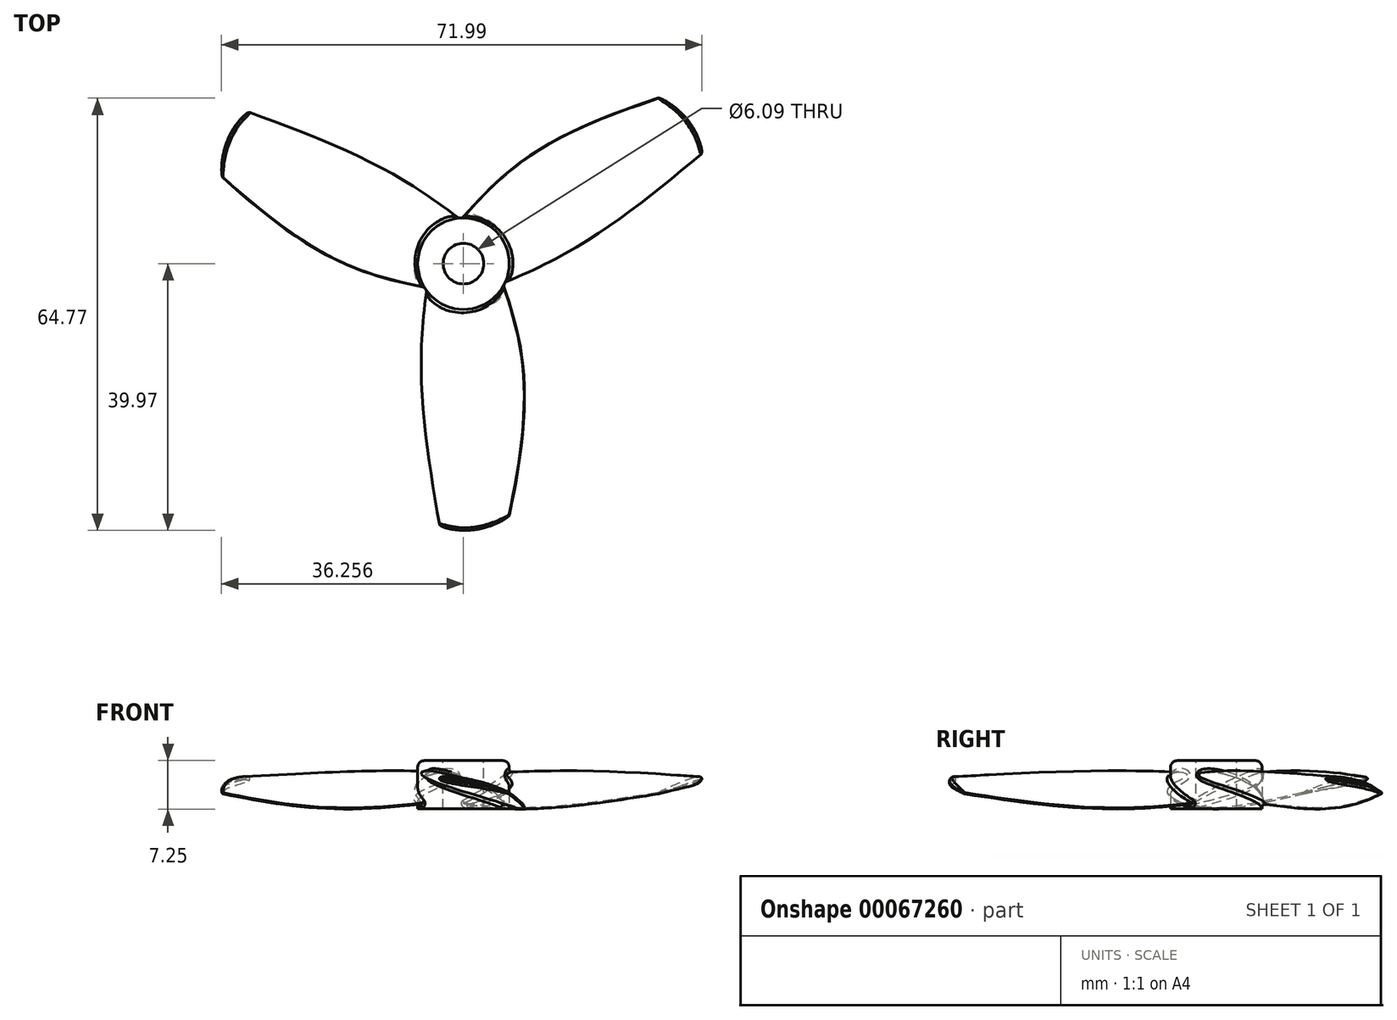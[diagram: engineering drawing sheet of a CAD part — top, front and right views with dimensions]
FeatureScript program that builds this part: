
annotation { "Feature Type Name" : "Feature", "Feature Type Description" : "" }
export const myFeature = defineFeature(function(context is Context, id is Id, definition is map)
    precondition{}
    {
        {
            var Q0;
            Q0=qCreatedBy(makeId("Front.planeOp"),FACE);
            var sketch = newSketch(context, id + "F0", { "sketchPlane" : qUnion([Q0])});
            skLineSegment(sketch, "E0", {"start": v(-25.68, 10.16) * mm, "end": v(0, 0) * mm, "construction": true});
            skLineSegment(sketch, "E1", {"start": v(0, 0) * mm, "end": v(25.68, -10.16) * mm, "construction": true});
            skLineSegment(sketch, "E2", {"start": v(25.68, -10.16) * mm, "end": v(51.36, -20.31) * mm, "construction": true});
            skLineSegment(sketch, "E3", {"start": v(51.36, -20.31) * mm, "end": v(77.03, -30.47) * mm, "construction": true});
            skLineSegment(sketch, "E4", {"start": v(0, 0) * mm, "end": v(3.73, 9.44) * mm, "construction": true});
            skLineSegment(sketch, "E5", {"start": v(-25.68, 10.16) * mm, "end": v(-23.81, 14.88) * mm, "construction": true});
            skFitSpline(sketch, "E6", {"points": [v(-25.68, 10.16) * mm, v(3.73, 9.44) * mm, v(77.03, -30.47) * mm], "startDerivative": vector(15.03, 38) * mm, "endDerivative": vector(104.92, -93.69) * mm});
            skPoint(sketch, "E7", {"position": v(1.87, 4.72) * mm});
            skLineSegment(sketch, "E8", {"start": v(-23.81, 14.88) * mm, "end": v(1.87, 4.72) * mm, "construction": true});
            skLineSegment(sketch, "E9", {"start": v(0, 0) * mm, "end": v(-1.87, -4.72) * mm, "construction": true});
            skLineSegment(sketch, "E10", {"start": v(-25.68, 10.16) * mm, "end": v(-27.54, 5.44) * mm, "construction": true});
            skFitSpline(sketch, "E11", {"points": [v(-25.68, 10.16) * mm, v(-1.87, -4.72) * mm, v(77.03, -30.47) * mm], "startDerivative": vector(-15.23, -38.5) * mm, "endDerivative": vector(121.84, -48.19) * mm});
            skLineSegment(sketch, "E12", {"start": v(51.36, -20.31) * mm, "end": v(55.09, -10.87) * mm, "construction": true});
            skSolve(sketch);
        }
        {
            var Q0;
            Q0=qCreatedBy(makeId("Front.planeOp"),FACE);
            cPlane(context, id + "F1", {"entities" : qUnion([Q0]), "cplaneType" : CPlaneType.OFFSET, "offset" : 125 * mm, "width" : 150 * mm, "height" : 150 * mm});
        }
        {
            var Q0;
            Q0=qCreatedBy(id+"F1.planeOp",FACE);
            var sketch = newSketch(context, id + "F2", { "sketchPlane" : qUnion([Q0])});
            skLineSegment(sketch, "E13", {"start": v(-38.33, 14.06) * mm, "end": v(0, 0) * mm, "construction": true});
            skLineSegment(sketch, "E14", {"start": v(0, 0) * mm, "end": v(38.33, -14.06) * mm, "construction": true});
            skLineSegment(sketch, "E15", {"start": v(38.33, -14.06) * mm, "end": v(76.67, -28.12) * mm, "construction": true});
            skLineSegment(sketch, "E16", {"start": v(76.67, -28.12) * mm, "end": v(115, -42.17) * mm, "construction": true});
            skLineSegment(sketch, "E17", {"start": v(0, 0) * mm, "end": v(4.06, 11.06) * mm, "construction": true});
            skLineSegment(sketch, "E18", {"start": v(-38.33, 14.06) * mm, "end": v(-36.3, 19.59) * mm, "construction": true});
            skFitSpline(sketch, "E19", {"points": [v(-38.33, 14.06) * mm, v(4.06, 11.06) * mm, v(115, -42.17) * mm], "startDerivative": vector(16.44, 44.82) * mm, "endDerivative": vector(163.27, -119.63) * mm});
            skPoint(sketch, "E20", {"position": v(2.03, 5.53) * mm});
            skLineSegment(sketch, "E21", {"start": v(-36.3, 19.59) * mm, "end": v(2.03, 5.53) * mm, "construction": true});
            skLineSegment(sketch, "E22", {"start": v(0, 0) * mm, "end": v(-2.03, -5.53) * mm, "construction": true});
            skLineSegment(sketch, "E23", {"start": v(-38.33, 14.06) * mm, "end": v(-40.36, 8.53) * mm, "construction": true});
            skFitSpline(sketch, "E24", {"points": [v(-38.33, 14.06) * mm, v(-2.03, -5.53) * mm, v(115, -42.17) * mm], "startDerivative": vector(-16.57, -45.19) * mm, "endDerivative": vector(181.7, -66.64) * mm});
            skLineSegment(sketch, "E25", {"start": v(76.67, -28.12) * mm, "end": v(80.72, -17.06) * mm, "construction": true});
            skSolve(sketch);
        }
        {
            var Q0;
            Q0=qCreatedBy(makeId("Front.planeOp"),FACE);
            cPlane(context, id + "F3", {"entities" : qUnion([Q0]), "cplaneType" : CPlaneType.OFFSET, "offset" : 400 * mm, "width" : 150 * mm, "height" : 150 * mm});
        }
        {
            var Q0;
            Q0=qCreatedBy(id+"F3.planeOp",FACE);
            var sketch = newSketch(context, id + "F4", { "sketchPlane" : qUnion([Q0])});
            skLineSegment(sketch, "E26", {"start": v(-10.03, 5.14) * mm, "end": v(16.27, 0) * mm, "construction": true});
            skLineSegment(sketch, "E27", {"start": v(16.27, 0) * mm, "end": v(42.56, -5.14) * mm, "construction": true});
            skLineSegment(sketch, "E28", {"start": v(42.56, -5.14) * mm, "end": v(68.86, -10.28) * mm, "construction": true});
            skLineSegment(sketch, "E29", {"start": v(68.86, -10.28) * mm, "end": v(95.16, -15.42) * mm, "construction": true});
            skLineSegment(sketch, "E30", {"start": v(16.27, 0) * mm, "end": v(17.61, 6.9) * mm, "construction": true});
            skLineSegment(sketch, "E31", {"start": v(-10.03, 5.14) * mm, "end": v(-9.36, 8.59) * mm, "construction": true});
            skFitSpline(sketch, "E32", {"points": [v(-10.03, 5.14) * mm, v(17.61, 6.9) * mm, v(95.16, -15.42) * mm], "startDerivative": vector(5.47, 28.01) * mm, "endDerivative": vector(118.7, -57.28) * mm});
            skPoint(sketch, "E33", {"position": v(16.94, 3.45) * mm});
            skLineSegment(sketch, "E34", {"start": v(-9.36, 8.59) * mm, "end": v(16.94, 3.45) * mm, "construction": true});
            skLineSegment(sketch, "E35", {"start": v(16.27, 0) * mm, "end": v(15.6, -3.45) * mm, "construction": true});
            skLineSegment(sketch, "E36", {"start": v(-10.03, 5.14) * mm, "end": v(-10.7, 1.7) * mm, "construction": true});
            skFitSpline(sketch, "E37", {"points": [v(-10.03, 5.14) * mm, v(15.6, -3.45) * mm, v(95.16, -15.42) * mm], "startDerivative": vector(-5.51, -28.2) * mm, "endDerivative": vector(124.61, -24.36) * mm});
            skLineSegment(sketch, "E38", {"start": v(68.86, -10.28) * mm, "end": v(70.2, -3.38) * mm, "construction": true});
            skSolve(sketch);
        }
        {
            var Q0;
            Q0=qSketchRegion(id+"F0",true);
            var Q1;
            Q1=qSketchRegion(id+"F2",true);
            var Q2;
            Q2=qSketchRegion(id+"F4",true);
            var Q3;
            Q3=sQuery(id+"F0.wireOp",VERTEX,"E6.1.internal");
            var Q4;
            Q4=sQuery(id+"F2.wireOp",VERTEX,"E19.1.internal");
            var Q5;
            Q5=sQuery(id+"F4.wireOp",VERTEX,"E30.end");
            loft(context, id + "F5", {"sheetProfilesArray" : [{ "sheetProfileEntities" : qUnion([Q0]) }, { "sheetProfileEntities" : qUnion([Q1]) }, { "sheetProfileEntities" : qUnion([Q2]) }], "matchConnections" : true, "connections" : [{ "connectionEntities" : qUnion([Q3, Q4, Q5]), "connectionEdgeQueries" : qUnion([]), "connectionEdgeParameters" : [] }]});
        }
        {
            var Q0;
            Q0=qCreatedBy(makeId("Top.planeOp"),FACE);
            var sketch = newSketch(context, id + "F6", { "sketchPlane" : qUnion([Q0])});
            skFitSpline(sketch, "E39", {"points": [v(-55.98, -360.47) * mm, v(39.38, -398.87) * mm, v(142.8, -333.19) * mm], "startDerivative": vector(111.22, -150.8) * mm, "endDerivative": vector(54.24, 145.78) * mm});
            skLineSegment(sketch, "E40", {"start": v(-55.98, -360.47) * mm, "end": v(-55.98, -458.75) * mm});
            skLineSegment(sketch, "E41", {"start": v(142.8, -333.19) * mm, "end": v(142.8, -458.75) * mm});
            skLineSegment(sketch, "E42", {"start": v(142.8, -458.75) * mm, "end": v(-55.98, -458.75) * mm});
            skSolve(sketch);
        }
        {
            var Q0;
            Q0=qSketchRegion(id+"F6",true);
            extrude(context, id + "F7", {"entities" : qUnion([Q0]), "operationType" : NewBodyOperationType.REMOVE, "endBound" : BoundingType.SYMMETRIC, "oppositeDirection" : true, "depth" : 40.17 * mm});
        }
        {
            var Q0;
            Q0=makeQuery(id+"F5.opLoft","SWEPT_EDGE",EDGE,{"disambiguationData":[OSD([sQuery(id+"F2.wireOp",EDGE,"E19"),sQuery(id+"F2.wireOp",EDGE,"E24"),sQuery(id+"F4.wireOp",EDGE,"E32"),sQuery(id+"F4.wireOp",EDGE,"E37")])]});
            fillet(context, id + "F8", {"entities" : qUnion([Q0]), "radius" : 1 * mm, "tangentPropagation" : true, "allowEdgeOverflow" : false});
        }
        {
            var Q0;
            Q0=makeQuery(id+"F7.boolean.opBoolean","COPY",FACE,{"derivedFrom":makeQuery(id+"F7.opExtrude","SWEPT_FACE",FACE,{"disambiguationData":[OSD([sQuery(id+"F6.wireOp",EDGE,"E39")])]})});
            fillet(context, id + "F9", {"entities" : qUnion([Q0]), "radius" : 4 * mm, "tangentPropagation" : true, "allowEdgeOverflow" : false});
        }
        {
            var Q0;
            Q0=qCreatedBy(makeId("Top.planeOp"),FACE);
            var sketch = newSketch(context, id + "F10", { "sketchPlane" : qUnion([Q0])});
            skCircle(sketch, "E43", {"center": v(24.35, 0) * mm, "radius": 68.6 * mm});
            skSolve(sketch);
        }
        {
            var Q0;
            Q0=qSketchRegion(id+"F10",true);
            extrude(context, id + "F11", {"entities" : qUnion([Q0]), "depth" : 32.31 * mm, "hasSecondDirection" : true, "secondDirectionOppositeDirection" : true, "secondDirectionDepth" : 40 * mm});
        }
        {
            var Q0;
            Q0=makeQuery(id+"F5.opLoft","SWEPT_BODY",BODY,{"disambiguationData":[OSD([makeQuery(id+"F0.imprint","IMPRINT",FACE,{"disambiguationData":[TD([[makeQuery(id+"F0.imprint","IMPRINT",EDGE,{"derivedFrom":sQuery(id+"F0.wireOp",EDGE,"E6")}),-1.0]])]}),sQuery(id+"F2.wireOp",EDGE,"E24"),makeQuery(id+"F4.imprint","IMPRINT",FACE,{"disambiguationData":[TD([[makeQuery(id+"F4.imprint","IMPRINT",EDGE,{"derivedFrom":sQuery(id+"F4.wireOp",EDGE,"E32")}),-1.0]])]})])]});
            var Q1;
            Q1=makeQuery(id+"F11.opExtrude","SWEPT_FACE",FACE,{"disambiguationData":[OSD([sQuery(id+"F10.wireOp",EDGE,"E43")])]});
            circularPattern(context, id + "F12", {"entities" : qUnion([Q0]), "axis" : qUnion([Q1]), "angle" : 360 * degree, "instanceCount" : round(3), "equalSpace" : true});
        }
        {
            var Q0;
            Q0=makeQuery(id+"F12.opPattern","COPY",BODY,{"derivedFrom":makeQuery(id+"F5.opLoft","SWEPT_BODY",BODY,{"disambiguationData":[OSD([makeQuery(id+"F0.imprint","IMPRINT",FACE,{"disambiguationData":[TD([[makeQuery(id+"F0.imprint","IMPRINT",EDGE,{"derivedFrom":sQuery(id+"F0.wireOp",EDGE,"E6")}),-1.0]])]}),sQuery(id+"F2.wireOp",EDGE,"E24"),makeQuery(id+"F4.imprint","IMPRINT",FACE,{"disambiguationData":[TD([[makeQuery(id+"F4.imprint","IMPRINT",EDGE,{"derivedFrom":sQuery(id+"F4.wireOp",EDGE,"E32")}),-1.0]])]})])]}),"instanceName":"2"});
            var Q1;
            Q1=makeQuery(id+"F5.opLoft","SWEPT_BODY",BODY,{"disambiguationData":[OSD([makeQuery(id+"F0.imprint","IMPRINT",FACE,{"disambiguationData":[TD([[makeQuery(id+"F0.imprint","IMPRINT",EDGE,{"derivedFrom":sQuery(id+"F0.wireOp",EDGE,"E6")}),-1.0]])]}),sQuery(id+"F2.wireOp",EDGE,"E24"),makeQuery(id+"F4.imprint","IMPRINT",FACE,{"disambiguationData":[TD([[makeQuery(id+"F4.imprint","IMPRINT",EDGE,{"derivedFrom":sQuery(id+"F4.wireOp",EDGE,"E32")}),-1.0]])]})])]});
            var Q2;
            Q2=makeQuery(id+"F11.opExtrude","SWEPT_BODY",BODY,{"disambiguationData":[OSD([sQuery(id+"F10.wireOp",EDGE,"E43")])]});
            var Q3;
            Q3=makeQuery(id+"F12.opPattern","COPY",BODY,{"derivedFrom":makeQuery(id+"F5.opLoft","SWEPT_BODY",BODY,{"disambiguationData":[OSD([makeQuery(id+"F0.imprint","IMPRINT",FACE,{"disambiguationData":[TD([[makeQuery(id+"F0.imprint","IMPRINT",EDGE,{"derivedFrom":sQuery(id+"F0.wireOp",EDGE,"E6")}),-1.0]])]}),sQuery(id+"F2.wireOp",EDGE,"E24"),makeQuery(id+"F4.imprint","IMPRINT",FACE,{"disambiguationData":[TD([[makeQuery(id+"F4.imprint","IMPRINT",EDGE,{"derivedFrom":sQuery(id+"F4.wireOp",EDGE,"E32")}),-1.0]])]})])]}),"instanceName":"1"});
            var Q4;
            Q4=makeQuery(id+"F12.opPattern","COPY",BODY,{"derivedFrom":makeQuery(id+"F5.opLoft","SWEPT_BODY",BODY,{"disambiguationData":[OSD([makeQuery(id+"F0.imprint","IMPRINT",FACE,{"disambiguationData":[TD([[makeQuery(id+"F0.imprint","IMPRINT",EDGE,{"derivedFrom":sQuery(id+"F0.wireOp",EDGE,"E6")}),-1.0]])]}),sQuery(id+"F2.wireOp",EDGE,"E24"),makeQuery(id+"F4.imprint","IMPRINT",FACE,{"disambiguationData":[TD([[makeQuery(id+"F4.imprint","IMPRINT",EDGE,{"derivedFrom":sQuery(id+"F4.wireOp",EDGE,"E32")}),-1.0]])]})])]}),"instanceName":"4"});
            var Q5;
            Q5=makeQuery(id+"F12.opPattern","COPY",BODY,{"derivedFrom":makeQuery(id+"F5.opLoft","SWEPT_BODY",BODY,{"disambiguationData":[OSD([makeQuery(id+"F0.imprint","IMPRINT",FACE,{"disambiguationData":[TD([[makeQuery(id+"F0.imprint","IMPRINT",EDGE,{"derivedFrom":sQuery(id+"F0.wireOp",EDGE,"E6")}),-1.0]])]}),sQuery(id+"F2.wireOp",EDGE,"E24"),makeQuery(id+"F4.imprint","IMPRINT",FACE,{"disambiguationData":[TD([[makeQuery(id+"F4.imprint","IMPRINT",EDGE,{"derivedFrom":sQuery(id+"F4.wireOp",EDGE,"E32")}),-1.0]])]})])]}),"instanceName":"3"});
            booleanBodies(context, id + "F13", {"operationType" : BooleanOperationType.UNION, "tools" : qUnion([Q0, Q1, Q2, Q3, Q4, Q5])});
        }
        {
            var Q0;
            Q0=makeQuery(id+"F11.opExtrude","CAP_FACE",FACE,{"disambiguationData":[OSD([sQuery(id+"F10.wireOp",EDGE,"E43")])],"isStart":false});
            var sketch = newSketch(context, id + "F14", { "sketchPlane" : qUnion([Q0])});
            skCircle(sketch, "E44", {"center": v(24.35, 0) * mm, "radius": 30.45 * mm});
            skSolve(sketch);
        }
        {
            var Q0;
            Q0=qSketchRegion(id+"F14",true);
            extrude(context, id + "F15", {"entities" : qUnion([Q0]), "operationType" : NewBodyOperationType.REMOVE, "endBound" : BoundingType.THROUGH_ALL, "oppositeDirection" : true, "depth" : 25 * mm});
        }
        {
            var Q0;
            {var subQ0=sQuery(id+"F0.wireOp",VERTEX,"E6.1.internal");var subQ1=sQuery(id+"F0.wireOp",EDGE,"E6");var subQ2=sQuery(id+"F0.wireOp",EDGE,"E11");var subQ3=sQuery(id+"F2.wireOp",VERTEX,"E19.1.internal");var subQ4=sQuery(id+"F2.wireOp",EDGE,"E19");var subQ5=sQuery(id+"F2.wireOp",EDGE,"E24");Q0=makeQuery(id+"F13.opBoolean","INTERSECT",EDGE,{"derivedFrom":[makeQuery(id+"F11.opExtrude","SWEPT_FACE",FACE,{"disambiguationData":[OSD([sQuery(id+"F10.wireOp",EDGE,"E43")])]}),makeQuery(id+"F12.opPattern","COPY",FACE,{"derivedFrom":makeQuery(id+"F5.opLoft","SWEPT_FACE",FACE,{"disambiguationData":[OSD([subQ0,subQ1,subQ2,subQ3,subQ4,subQ5]),TDD([subQ0,makeQuery(id+"F0.imprint","INTERSECT",VERTEX,{"disambiguationData":[OD(0.0)],"derivedFrom":[subQ1,subQ2]}),makeQuery(id+"F0.imprint","IMPRINT",EDGE,{"derivedFrom":subQ1}),subQ3,makeQuery(id+"F2.imprint","INTERSECT",VERTEX,{"disambiguationData":[OD(0.0)],"derivedFrom":[subQ4,subQ5]}),makeQuery(id+"F2.imprint","IMPRINT",EDGE,{"derivedFrom":subQ4})])]}),"instanceName":"2"})]});}
            var Q1;
            {var subQ0=sQuery(id+"F0.wireOp",VERTEX,"E6.1.internal");var subQ1=sQuery(id+"F0.wireOp",EDGE,"E6");var subQ2=sQuery(id+"F0.wireOp",EDGE,"E11");var subQ3=sQuery(id+"F2.wireOp",VERTEX,"E19.1.internal");var subQ4=sQuery(id+"F2.wireOp",EDGE,"E19");var subQ5=sQuery(id+"F2.wireOp",EDGE,"E24");Q1=makeQuery(id+"F13.opBoolean","INTERSECT",EDGE,{"derivedFrom":[makeQuery(id+"F5.opLoft","SWEPT_FACE",FACE,{"disambiguationData":[OSD([subQ0,subQ1,subQ2,subQ3,subQ4,subQ5]),TDD([subQ0,makeQuery(id+"F0.imprint","INTERSECT",VERTEX,{"disambiguationData":[OD(1.0)],"derivedFrom":[subQ1,subQ2]}),makeQuery(id+"F0.imprint","IMPRINT",EDGE,{"derivedFrom":subQ1}),subQ3,makeQuery(id+"F2.imprint","INTERSECT",VERTEX,{"disambiguationData":[OD(1.0)],"derivedFrom":[subQ4,subQ5]}),makeQuery(id+"F2.imprint","IMPRINT",EDGE,{"derivedFrom":subQ4})])]}),makeQuery(id+"F11.opExtrude","SWEPT_FACE",FACE,{"disambiguationData":[OSD([sQuery(id+"F10.wireOp",EDGE,"E43")])]})]});}
            var Q2;
            {var subQ0=sQuery(id+"F0.wireOp",VERTEX,"E6.1.internal");var subQ1=sQuery(id+"F0.wireOp",EDGE,"E6");var subQ2=sQuery(id+"F0.wireOp",EDGE,"E11");var subQ3=sQuery(id+"F2.wireOp",VERTEX,"E19.1.internal");var subQ4=sQuery(id+"F2.wireOp",EDGE,"E19");var subQ5=sQuery(id+"F2.wireOp",EDGE,"E24");Q2=makeQuery(id+"F13.opBoolean","INTERSECT",EDGE,{"derivedFrom":[makeQuery(id+"F11.opExtrude","SWEPT_FACE",FACE,{"disambiguationData":[OSD([sQuery(id+"F10.wireOp",EDGE,"E43")])]}),makeQuery(id+"F12.opPattern","COPY",FACE,{"derivedFrom":makeQuery(id+"F5.opLoft","SWEPT_FACE",FACE,{"disambiguationData":[OSD([subQ0,subQ1,subQ2,subQ3,subQ4,subQ5]),TDD([subQ0,makeQuery(id+"F0.imprint","INTERSECT",VERTEX,{"disambiguationData":[OD(1.0)],"derivedFrom":[subQ1,subQ2]}),makeQuery(id+"F0.imprint","IMPRINT",EDGE,{"derivedFrom":subQ1}),subQ3,makeQuery(id+"F2.imprint","INTERSECT",VERTEX,{"disambiguationData":[OD(1.0)],"derivedFrom":[subQ4,subQ5]}),makeQuery(id+"F2.imprint","IMPRINT",EDGE,{"derivedFrom":subQ4})])]}),"instanceName":"1"})]});}
            var Q3;
            {var subQ0=sQuery(id+"F0.wireOp",VERTEX,"E6.1.internal");var subQ1=sQuery(id+"F0.wireOp",EDGE,"E6");var subQ2=sQuery(id+"F0.wireOp",EDGE,"E11");var subQ3=sQuery(id+"F2.wireOp",VERTEX,"E19.1.internal");var subQ4=sQuery(id+"F2.wireOp",EDGE,"E19");var subQ5=sQuery(id+"F2.wireOp",EDGE,"E24");Q3=makeQuery(id+"F13.opBoolean","INTERSECT",EDGE,{"derivedFrom":[makeQuery(id+"F11.opExtrude","SWEPT_FACE",FACE,{"disambiguationData":[OSD([sQuery(id+"F10.wireOp",EDGE,"E43")])]}),makeQuery(id+"F12.opPattern","COPY",FACE,{"derivedFrom":makeQuery(id+"F5.opLoft","SWEPT_FACE",FACE,{"disambiguationData":[OSD([subQ0,subQ1,subQ2,subQ3,subQ4,subQ5]),TDD([subQ0,makeQuery(id+"F0.imprint","INTERSECT",VERTEX,{"disambiguationData":[OD(1.0)],"derivedFrom":[subQ1,subQ2]}),makeQuery(id+"F0.imprint","IMPRINT",EDGE,{"derivedFrom":subQ1}),subQ3,makeQuery(id+"F2.imprint","INTERSECT",VERTEX,{"disambiguationData":[OD(1.0)],"derivedFrom":[subQ4,subQ5]}),makeQuery(id+"F2.imprint","IMPRINT",EDGE,{"derivedFrom":subQ4})])]}),"instanceName":"4"})]});}
            var Q4;
            {var subQ0=sQuery(id+"F0.wireOp",VERTEX,"E6.1.internal");var subQ1=sQuery(id+"F0.wireOp",EDGE,"E6");var subQ2=sQuery(id+"F0.wireOp",EDGE,"E11");var subQ3=sQuery(id+"F2.wireOp",VERTEX,"E19.1.internal");var subQ4=sQuery(id+"F2.wireOp",EDGE,"E19");var subQ5=sQuery(id+"F2.wireOp",EDGE,"E24");Q4=makeQuery(id+"F13.opBoolean","INTERSECT",EDGE,{"derivedFrom":[makeQuery(id+"F11.opExtrude","SWEPT_FACE",FACE,{"disambiguationData":[OSD([sQuery(id+"F10.wireOp",EDGE,"E43")])]}),makeQuery(id+"F12.opPattern","COPY",FACE,{"derivedFrom":makeQuery(id+"F5.opLoft","SWEPT_FACE",FACE,{"disambiguationData":[OSD([subQ0,subQ1,subQ2,subQ3,subQ4,subQ5]),TDD([subQ0,makeQuery(id+"F0.imprint","INTERSECT",VERTEX,{"disambiguationData":[OD(0.0)],"derivedFrom":[subQ1,subQ2]}),makeQuery(id+"F0.imprint","IMPRINT",EDGE,{"derivedFrom":subQ1}),subQ3,makeQuery(id+"F2.imprint","INTERSECT",VERTEX,{"disambiguationData":[OD(0.0)],"derivedFrom":[subQ4,subQ5]}),makeQuery(id+"F2.imprint","IMPRINT",EDGE,{"derivedFrom":subQ4})])]}),"instanceName":"3"})]});}
            fillet(context, id + "F16", {"entities" : qUnion([Q0, Q1, Q2, Q3, Q4]), "radius" : 5 * mm, "tangentPropagation" : true, "allowEdgeOverflow" : false});
        }
        {
            var Q0;
            Q0=makeQuery(id+"F11.opExtrude","CAP_EDGE",EDGE,{"disambiguationData":[OSD([sQuery(id+"F10.wireOp",EDGE,"E43")])],"isStart":false});
            fillet(context, id + "F17", {"entities" : qUnion([Q0]), "radius" : 10 * mm, "tangentPropagation" : true, "allowEdgeOverflow" : false});
        }
        {
            var Q0;
            Q0=makeQuery(id+"F12.opPattern","COPY",BODY,{"derivedFrom":makeQuery(id+"F5.opLoft","SWEPT_BODY",BODY,{"disambiguationData":[OSD([makeQuery(id+"F0.imprint","IMPRINT",FACE,{"disambiguationData":[TD([[makeQuery(id+"F0.imprint","IMPRINT",EDGE,{"derivedFrom":sQuery(id+"F0.wireOp",EDGE,"E6")}),-1.0]])]}),sQuery(id+"F2.wireOp",EDGE,"E19"),makeQuery(id+"F4.imprint","IMPRINT",FACE,{"disambiguationData":[TD([[makeQuery(id+"F4.imprint","IMPRINT",EDGE,{"derivedFrom":sQuery(id+"F4.wireOp",EDGE,"E32")}),-1.0]])]})])]}),"instanceName":"2"});
            var Q1;
            Q1=sQuery(id+"F10.wireOp",VERTEX,"E43.center");
            transform(context, id + "F18", {"entities" : qUnion([Q0]), "transformType" : TransformType.SCALE_UNIFORMLY, "scale" : 0.1, "scalePoint" : qUnion([Q1]), "makeCopy" : false});
        }
    });
